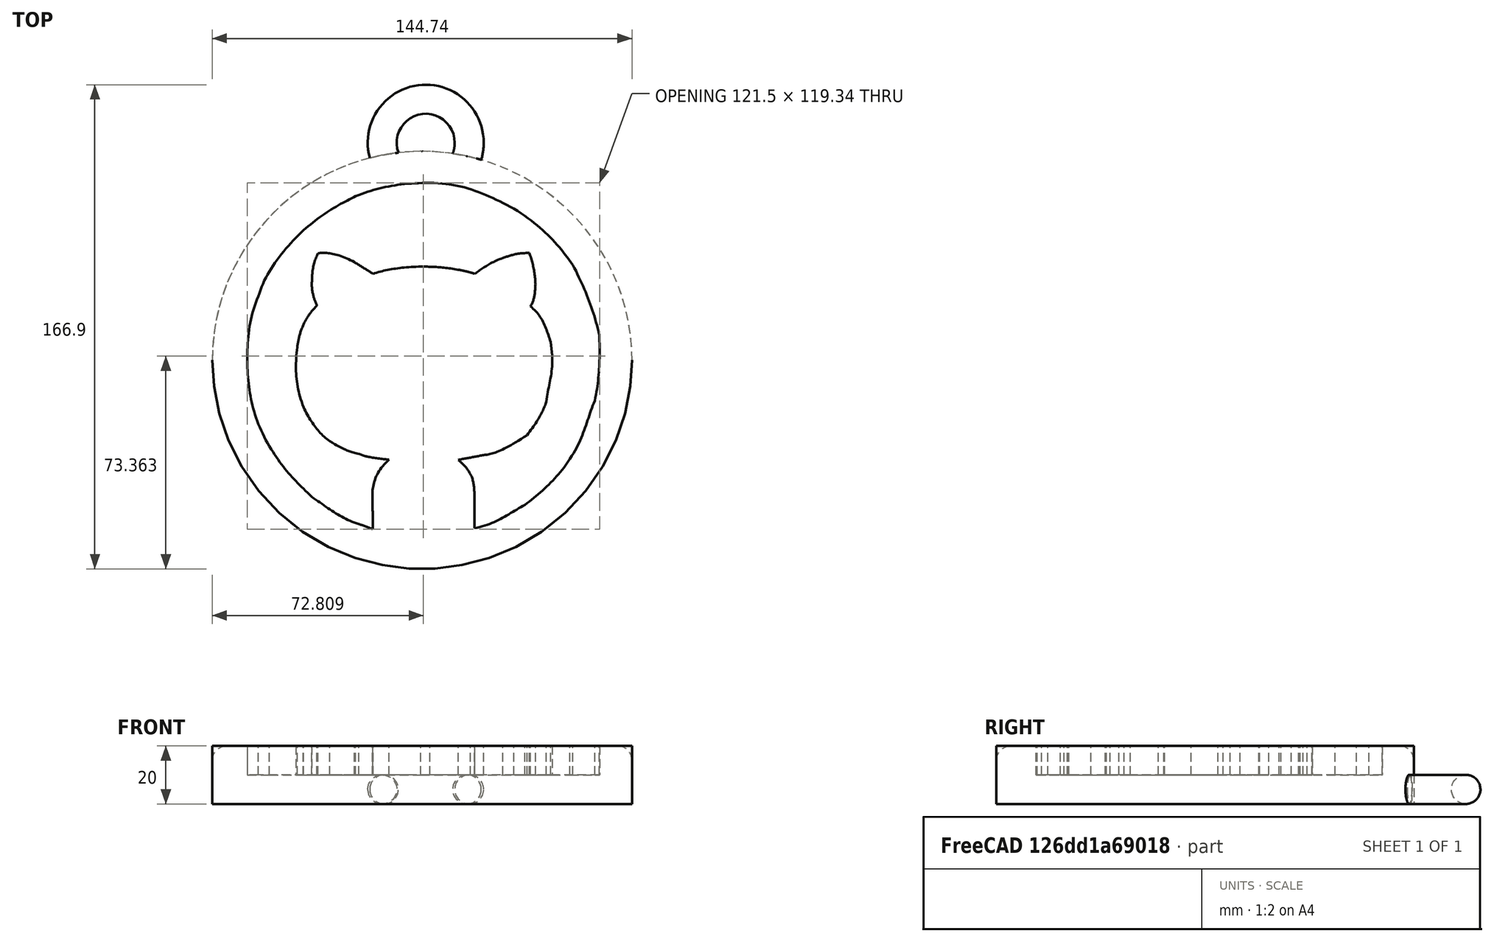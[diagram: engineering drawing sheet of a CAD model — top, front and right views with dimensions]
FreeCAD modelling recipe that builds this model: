
FCSTD DOCUMENT  (FreeCAD 0.15R4614 (Git))
Label: logo-GitHub
License: CC-BY 3.0
LicenseURL: http://creativecommons.org/licenses/by/3.0/
objects: Part::Feature×4, Part::Extrusion×2, Part::Cut×1, PartDesign::Fillet×1, Part::Torus×1, Part::Fuse×1
note: 10 computed .brp shape members not serialized (recipe doc carries the construction recipe); baked Part::Feature solids carry a one-line shape summary decoded from their .brp

FEATURE [Part::Feature] path2997
  shape: bbox 121.9 x 119.5 x 2e-07 mm, 0 faces, 0 solids (baked)
FEATURE [Part::Feature] path3771
  shape: bbox 144.7 x 143.9 x 2.006e-07 mm, 0 faces, 0 solids (baked)
FEATURE [Part::Extrusion] Extrude
  Base = -> path3771
  Dir = (0,0,20)
  Solid = true
FEATURE [Part::Extrusion] Extrude001
  Base = -> path2997
  Dir = (0,0,10)
  Placement = pos=(0,0,10) rot=(0,0,1;0rad)
  Solid = true
FEATURE [Part::Cut] Cut
  Base = -> Extrude
  Tool = -> Extrude001
FEATURE [Part::Feature] Cut001
  shape: bbox 144.7 x 143.9 x 20 mm, 48 faces (baked)
FEATURE [PartDesign::Fillet] Fillet
  Base = -> Cut001 [Edge6,Edge4]
  Radius = 5
FEATURE [Part::Torus] Torus  label="Toro"
  Angle1 = -180
  Angle2 = 180
  Angle3 = 360
  Placement = pos=(0,79,5) rot=(0,0,1;0rad)
  Radius1 = 15
  Radius2 = 5
FEATURE [Part::Fuse] Fusion
  Base = -> Fillet
  Tool = -> Torus
FEATURE [Part::Feature] Fusion001
  shape: bbox 144.7 x 168.5 x 20 mm, 52 faces (baked)
